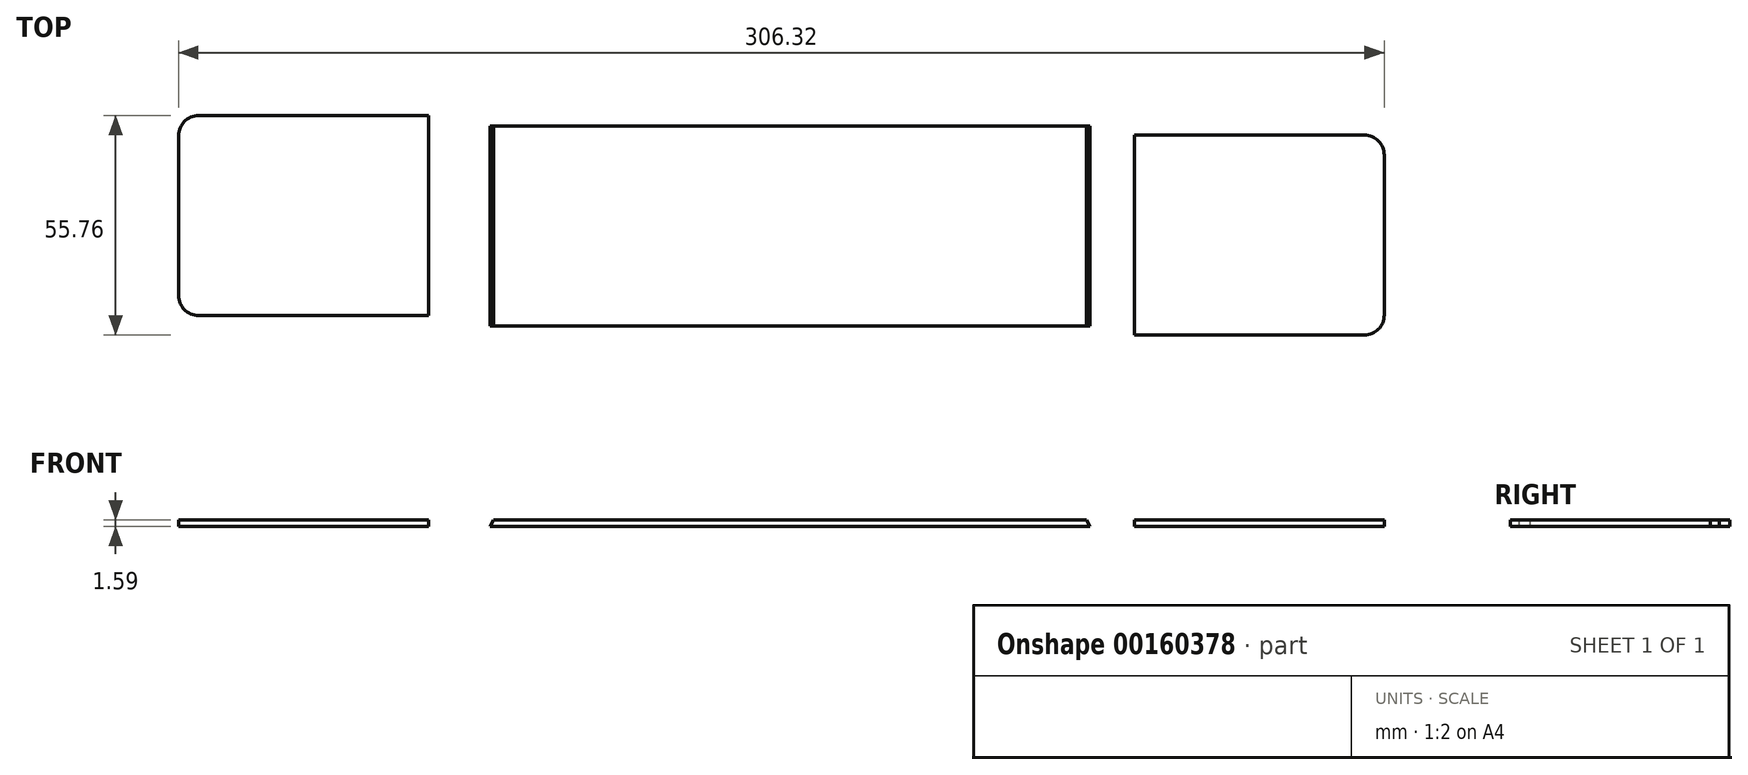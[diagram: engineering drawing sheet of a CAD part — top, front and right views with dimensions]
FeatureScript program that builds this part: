
annotation { "Feature Type Name" : "Feature", "Feature Type Description" : "" }
export const myFeature = defineFeature(function(context is Context, id is Id, definition is map)
    precondition{}
    {
        {
            var Q0;
            Q0=qCreatedBy(makeId("Top.planeOp"),FACE);
            var sketch = newSketch(context, id + "F0", { "sketchPlane" : qUnion([Q0])});
            skLineSegment(sketch, "E0.bottom", {"start": v(29.9, 1.22) * mm, "end": v(-122.5, 1.22) * mm});
            skLineSegment(sketch, "E0.top", {"start": v(29.9, 52.02) * mm, "end": v(-122.5, 52.02) * mm});
            skLineSegment(sketch, "E0.left", {"start": v(29.9, 1.22) * mm, "end": v(29.9, 52.02) * mm});
            skLineSegment(sketch, "E0.right", {"start": v(-122.5, 1.22) * mm, "end": v(-122.5, 52.02) * mm});
            skPoint(sketch, "E0.middle", {"position": v(-46.3, 26.62) * mm});
            skSolve(sketch);
        }
        {
            var Q0;
            Q0 = qSketchRegion(id + "F0", true);
            extrude(context, id + "F1", {"entities" : qUnion([Q0]), "depth" : 1.59 * mm});
        }
        {
            var Q0;
            Q0=qCreatedBy(makeId("Top.planeOp"),FACE);
            var sketch = newSketch(context, id + "F2", { "sketchPlane" : qUnion([Q0])});
            skLineSegment(sketch, "E1.bottom", {"start": v(104.64, -1.12) * mm, "end": v(41.14, -1.12) * mm});
            skLineSegment(sketch, "E1.top", {"start": v(104.64, 49.68) * mm, "end": v(41.14, 49.68) * mm});
            skLineSegment(sketch, "E1.left", {"start": v(104.64, -1.12) * mm, "end": v(104.64, 49.68) * mm});
            skLineSegment(sketch, "E1.right", {"start": v(41.14, -1.12) * mm, "end": v(41.14, 49.68) * mm});
            skPoint(sketch, "E1.middle", {"position": v(72.89, 24.28) * mm});
            skSolve(sketch);
        }
        {
            var Q0;
            Q0 = qSketchRegion(id + "F2", true);
            extrude(context, id + "F3", {"entities" : qUnion([Q0]), "depth" : 1.59 * mm});
        }
        {
            var Q0;
            Q0=makeQuery(id+"F1.opExtrude","SWEPT_FACE",FACE,{"disambiguationData":[OSD([sQuery(id+"F0.wireOp",EDGE,"E0.bottom")])]});
            var sketch = newSketch(context, id + "F4", { "sketchPlane" : qUnion([Q0])});
            skLineSegment(sketch, "E2", {"start": v(29.9, 0) * mm, "end": v(28.98, 1.59) * mm});
            skLineSegment(sketch, "E3", {"start": v(28.98, 1.59) * mm, "end": v(29.9, 1.59) * mm});
            skLineSegment(sketch, "E4", {"start": v(29.9, 1.59) * mm, "end": v(29.9, 0) * mm});
            skSolve(sketch);
        }
        {
            var Q0;
            Q0 = qSketchRegion(id + "F4", true);
            extrude(context, id + "F5", {"entities" : qUnion([Q0]), "operationType" : NewBodyOperationType.REMOVE, "endBound" : BoundingType.THROUGH_ALL, "oppositeDirection" : true, "depth" : 25.4 * mm});
        }
        {
            var Q0;
            Q0=makeQuery(id+"F3.opExtrude","SWEPT_EDGE",EDGE,{"disambiguationData":[OSD([sQuery(id+"F2.wireOp",EDGE,"E1.bottom"),sQuery(id+"F2.wireOp",EDGE,"E1.left")])]});
            var Q1;
            Q1=makeQuery(id+"F3.opExtrude","SWEPT_EDGE",EDGE,{"disambiguationData":[OSD([sQuery(id+"F2.wireOp",EDGE,"E1.top"),sQuery(id+"F2.wireOp",EDGE,"E1.left")])]});
            fillet(context, id + "F6", {"entities" : qUnion([Q0, Q1]), "radius" : 5.08 * mm, "tangentPropagation" : true, "allowEdgeOverflow" : false});
        }
        {
            var Q0;
            Q0=makeQuery(id+"F1.opExtrude","SWEPT_FACE",FACE,{"disambiguationData":[OSD([sQuery(id+"F0.wireOp",EDGE,"E0.bottom")])]});
            var sketch = newSketch(context, id + "F7", { "sketchPlane" : qUnion([Q0])});
            skLineSegment(sketch, "E5", {"start": v(-122.5, 0) * mm, "end": v(-121.58, 1.59) * mm});
            skLineSegment(sketch, "E6", {"start": v(-121.58, 1.59) * mm, "end": v(-122.5, 1.59) * mm});
            skLineSegment(sketch, "E7", {"start": v(-122.5, 1.59) * mm, "end": v(-122.5, 0) * mm});
            skSolve(sketch);
        }
        {
            var Q0;
            Q0 = qSketchRegion(id + "F7", true);
            extrude(context, id + "F8", {"entities" : qUnion([Q0]), "operationType" : NewBodyOperationType.REMOVE, "endBound" : BoundingType.THROUGH_ALL, "oppositeDirection" : true, "depth" : 25.4 * mm});
        }
        {
            var Q0;
            Q0=qCreatedBy(makeId("Top.planeOp"),FACE);
            var sketch = newSketch(context, id + "F9", { "sketchPlane" : qUnion([Q0])});
            skLineSegment(sketch, "E8.bottom", {"start": v(-138.18, 3.84) * mm, "end": v(-201.68, 3.84) * mm});
            skLineSegment(sketch, "E8.top", {"start": v(-138.18, 54.64) * mm, "end": v(-201.68, 54.64) * mm});
            skLineSegment(sketch, "E8.left", {"start": v(-138.18, 3.84) * mm, "end": v(-138.18, 54.64) * mm});
            skLineSegment(sketch, "E8.right", {"start": v(-201.68, 3.84) * mm, "end": v(-201.68, 54.64) * mm});
            skPoint(sketch, "E8.middle", {"position": v(-169.93, 29.24) * mm});
            skSolve(sketch);
        }
        {
            var Q0;
            Q0 = qSketchRegion(id + "F9", true);
            extrude(context, id + "F10", {"entities" : qUnion([Q0]), "depth" : 1.59 * mm});
        }
        {
            var Q0;
            Q0=makeQuery(id+"F10.opExtrude","SWEPT_EDGE",EDGE,{"disambiguationData":[OSD([sQuery(id+"F9.wireOp",EDGE,"E8.bottom"),sQuery(id+"F9.wireOp",EDGE,"E8.right")])]});
            var Q1;
            Q1=makeQuery(id+"F10.opExtrude","SWEPT_EDGE",EDGE,{"disambiguationData":[OSD([sQuery(id+"F9.wireOp",EDGE,"E8.top"),sQuery(id+"F9.wireOp",EDGE,"E8.right")])]});
            fillet(context, id + "F11", {"entities" : qUnion([Q0, Q1]), "radius" : 5.08 * mm, "tangentPropagation" : true, "allowEdgeOverflow" : false});
        }
    });
